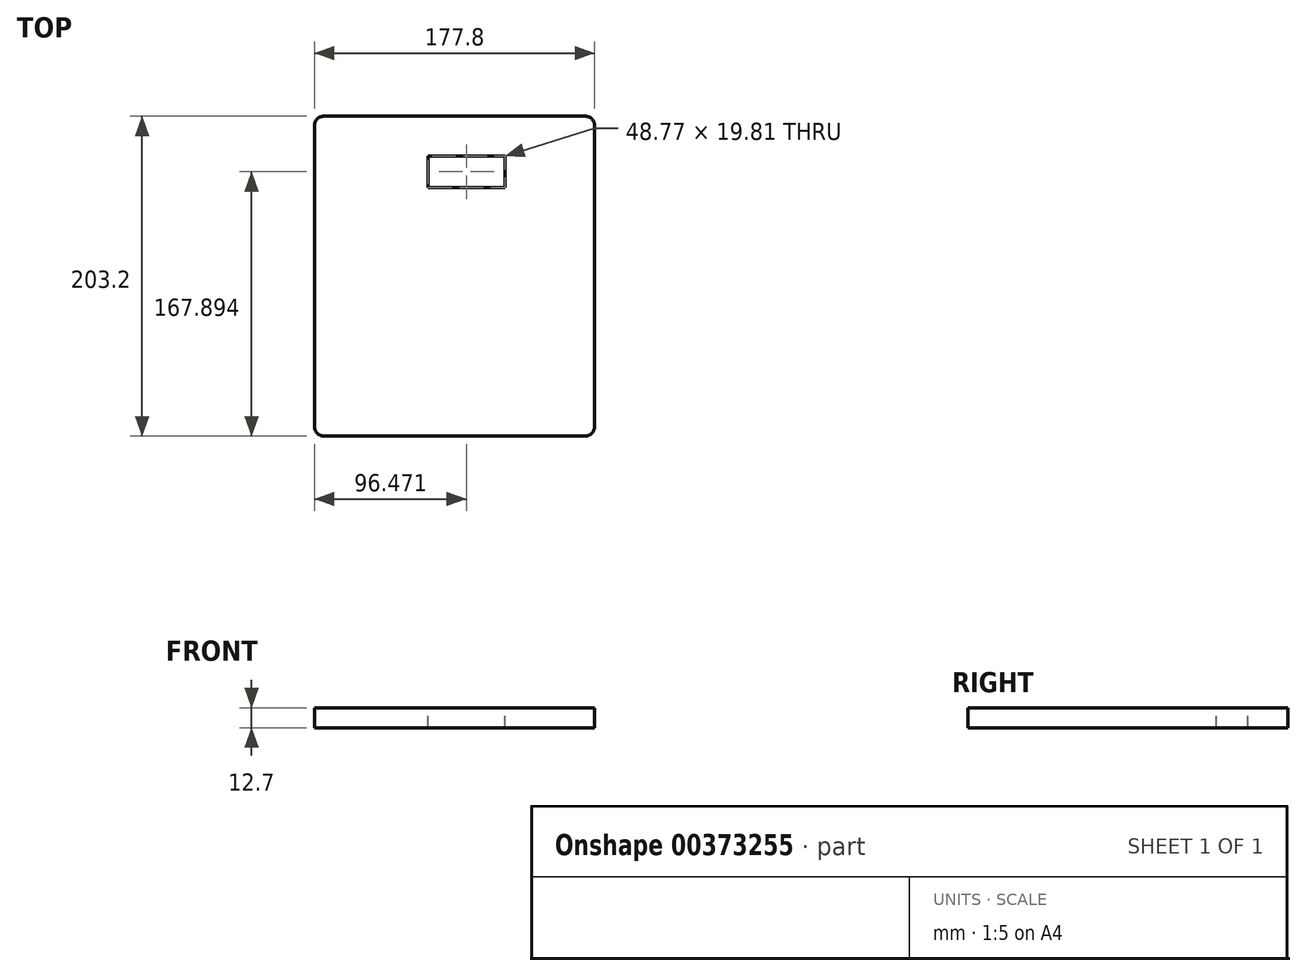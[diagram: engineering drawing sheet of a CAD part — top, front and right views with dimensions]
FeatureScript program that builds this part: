
annotation { "Feature Type Name" : "Feature", "Feature Type Description" : "" }
export const myFeature = defineFeature(function(context is Context, id is Id, definition is map)
    precondition{}
    {
        {
            var Q0;
            Q0=qCreatedBy(makeId("Top.planeOp"),FACE);
            var sketch = newSketch(context, id + "F0", { "sketchPlane" : qUnion([Q0])});
            skLineSegment(sketch, "E0.bottom", {"start": v(-43.86, 170.82) * mm, "end": v(122.13, 170.82) * mm});
            skLineSegment(sketch, "E0.top", {"start": v(-43.86, -32.38) * mm, "end": v(122.13, -32.38) * mm});
            skLineSegment(sketch, "E0.left", {"start": v(-49.76, 164.92) * mm, "end": v(-49.76, -26.48) * mm});
            skLineSegment(sketch, "E0.right", {"start": v(128.04, 164.92) * mm, "end": v(128.04, -26.48) * mm});
            skPoint(sketch, "E1.visualSharp", {"position": v(-49.76, 170.82) * mm});
            skArc(sketch, "E1.filletArc", {"start": v(-43.86, 170.82) * mm, "mid": v(-48.03, 169.1) * mm, "end": v(-49.76, 164.92) * mm});
            skPoint(sketch, "E2.visualSharp", {"position": v(128.04, 170.82) * mm});
            skArc(sketch, "E2.filletArc", {"start": v(128.04, 164.92) * mm, "mid": v(126.3, 169.1) * mm, "end": v(122.13, 170.82) * mm});
            skPoint(sketch, "E3.visualSharp", {"position": v(128.04, -32.38) * mm});
            skArc(sketch, "E3.filletArc", {"start": v(122.13, -32.38) * mm, "mid": v(126.3, -30.65) * mm, "end": v(128.04, -26.48) * mm});
            skPoint(sketch, "E4.visualSharp", {"position": v(-49.76, -32.38) * mm});
            skArc(sketch, "E4.filletArc", {"start": v(-49.76, -26.48) * mm, "mid": v(-48.03, -30.65) * mm, "end": v(-43.86, -32.38) * mm});
            skLineSegment(sketch, "E5.bottom", {"start": v(22.33, 145.42) * mm, "end": v(71.1, 145.42) * mm});
            skLineSegment(sketch, "E5.top", {"start": v(22.33, 125.6) * mm, "end": v(71.1, 125.6) * mm});
            skLineSegment(sketch, "E5.left", {"start": v(22.33, 145.42) * mm, "end": v(22.33, 125.6) * mm});
            skLineSegment(sketch, "E5.right", {"start": v(71.1, 145.42) * mm, "end": v(71.1, 125.6) * mm});
            skSolve(sketch);
        }
        {
            var Q0;
            Q0 = qSketchRegion(id + "F0", true);
            extrude(context, id + "F1", {"entities" : qUnion([Q0]), "oppositeDirection" : true, "depth" : 12.7 * mm});
        }
    });
